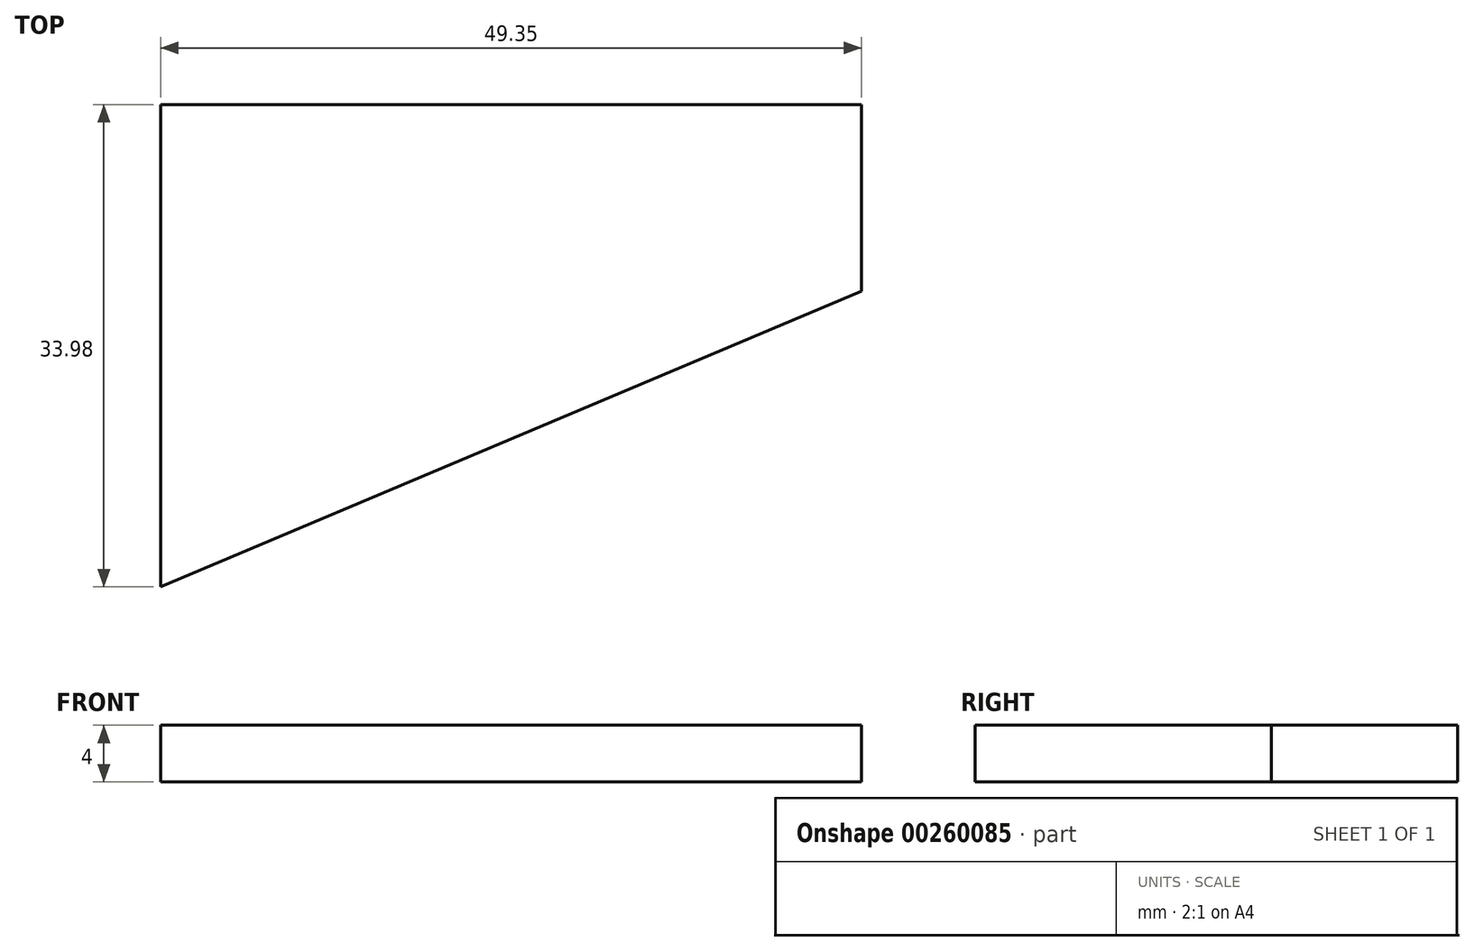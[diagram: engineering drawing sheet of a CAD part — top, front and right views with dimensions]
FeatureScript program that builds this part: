
annotation { "Feature Type Name" : "Feature", "Feature Type Description" : "" }
export const myFeature = defineFeature(function(context is Context, id is Id, definition is map)
    precondition{}
    {
        {
            var Q0;
            Q0=qCreatedBy(makeId("Top.planeOp"),FACE);
            var sketch = newSketch(context, id + "F0", { "sketchPlane" : qUnion([Q0])});
            skLineSegment(sketch, "E0.left", {"start": v(-90, 279.6) * mm, "end": v(-90, 245.62) * mm});
            skLineSegment(sketch, "E0.right", {"start": v(0, 245.62) * mm, "end": v(0, -152.38) * mm});
            skLineSegment(sketch, "E1.bottom", {"start": v(-91.3, 279.6) * mm, "end": v(-40.65, 279.6) * mm});
            skLineSegment(sketch, "E1.top", {"start": v(-90, 173.94) * mm, "end": v(-40.65, 173.94) * mm});
            skLineSegment(sketch, "E1.right", {"start": v(-40.65, 279.6) * mm, "end": v(-40.65, 173.94) * mm});
            skLineSegment(sketch, "E2.trimOffspring", {"start": v(-90, 173.94) * mm, "end": v(-90, -8.06) * mm});
            skLineSegment(sketch, "E3.bottom", {"start": v(-90.65, -8.06) * mm, "end": v(-40, -8.06) * mm});
            skLineSegment(sketch, "E3.top", {"start": v(-90, -78.06) * mm, "end": v(-40, -78.06) * mm});
            skLineSegment(sketch, "E3.right", {"start": v(-40, -8.06) * mm, "end": v(-40, -78.06) * mm});
            skLineSegment(sketch, "E4.trimOffspring", {"start": v(-90, -78.06) * mm, "end": v(-90, -152.38) * mm});
            skLineSegment(sketch, "E5.MirrorCS", {"start": v(91.3, 279.6) * mm, "end": v(40.65, 279.6) * mm});
            skLineSegment(sketch, "E6.MirrorCS", {"start": v(90, 279.6) * mm, "end": v(90, 245.62) * mm});
            skLineSegment(sketch, "E7.MirrorCS", {"start": v(40.65, 279.6) * mm, "end": v(40.65, 173.94) * mm});
            skLineSegment(sketch, "E8.MirrorCS", {"start": v(90, 173.94) * mm, "end": v(40.65, 173.94) * mm});
            skLineSegment(sketch, "E9.MirrorCS", {"start": v(90, 173.94) * mm, "end": v(90, -8.06) * mm});
            skLineSegment(sketch, "E10.MirrorCS", {"start": v(90.65, -8.06) * mm, "end": v(40, -8.06) * mm});
            skLineSegment(sketch, "E11.MirrorCS", {"start": v(40, -8.06) * mm, "end": v(40, -78.06) * mm});
            skLineSegment(sketch, "E12.MirrorCS", {"start": v(90, -78.06) * mm, "end": v(40, -78.06) * mm});
            skLineSegment(sketch, "E13.MirrorCS", {"start": v(90, -78.06) * mm, "end": v(90, -152.38) * mm});
            skLineSegment(sketch, "E14", {"start": v(-90, 245.62) * mm, "end": v(0, 283.62) * mm});
            skLineSegment(sketch, "E15", {"start": v(0, 283.62) * mm, "end": v(90, 245.62) * mm});
            skPoint(sketch, "E16.MirrorCS.end.orphan", {"position": v(0, 245.62) * mm});
            skLineSegment(sketch, "E17", {"start": v(-90, -152.38) * mm, "end": v(0, -176.38) * mm});
            skLineSegment(sketch, "E18", {"start": v(0, -176.38) * mm, "end": v(90, -152.38) * mm});
            skPoint(sketch, "E19.MirrorCS.end.orphan", {"position": v(0, -152.38) * mm});
            skPoint(sketch, "E19.MirrorCS.start.orphan", {"position": v(90, -152.38) * mm});
            skSolve(sketch);
        }
        {
            var Q0;
            {var subQ1=sQuery(id+"F0.wireOp",EDGE,"E0.left");Q0=makeQuery(id+"F0.imprint","IMPRINT",FACE,{"disambiguationData":[TD([[makeQuery(id+"F0.imprint","IMPRINT",EDGE,{"derivedFrom":subQ1}),1.0]])]});}
            extrude(context, id + "F1", {"entities" : qUnion([Q0]), "depth" : 4 * mm});
        }
    });
